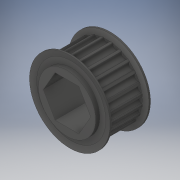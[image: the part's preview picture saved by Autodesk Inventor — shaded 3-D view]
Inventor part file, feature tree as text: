
AUTODESK INVENTOR PART (.ipt)
format: ipt  version: 2017 (Build 210142000, 142)  size: 367,616 bytes
history: native  units: in
note: dims shown in document units (in); Inventor stores cm internally (conversion verified against a paired STEP export)
features: mirror x1
ambient origin geometry x8: Origin, YZ Plane, XZ Plane, XY Plane, X Axis, Y Axis, Z Axis, Center Point
bodies: Solid1 (feature_tree)
feature tree (1):
  mirror  "Mirror1"
